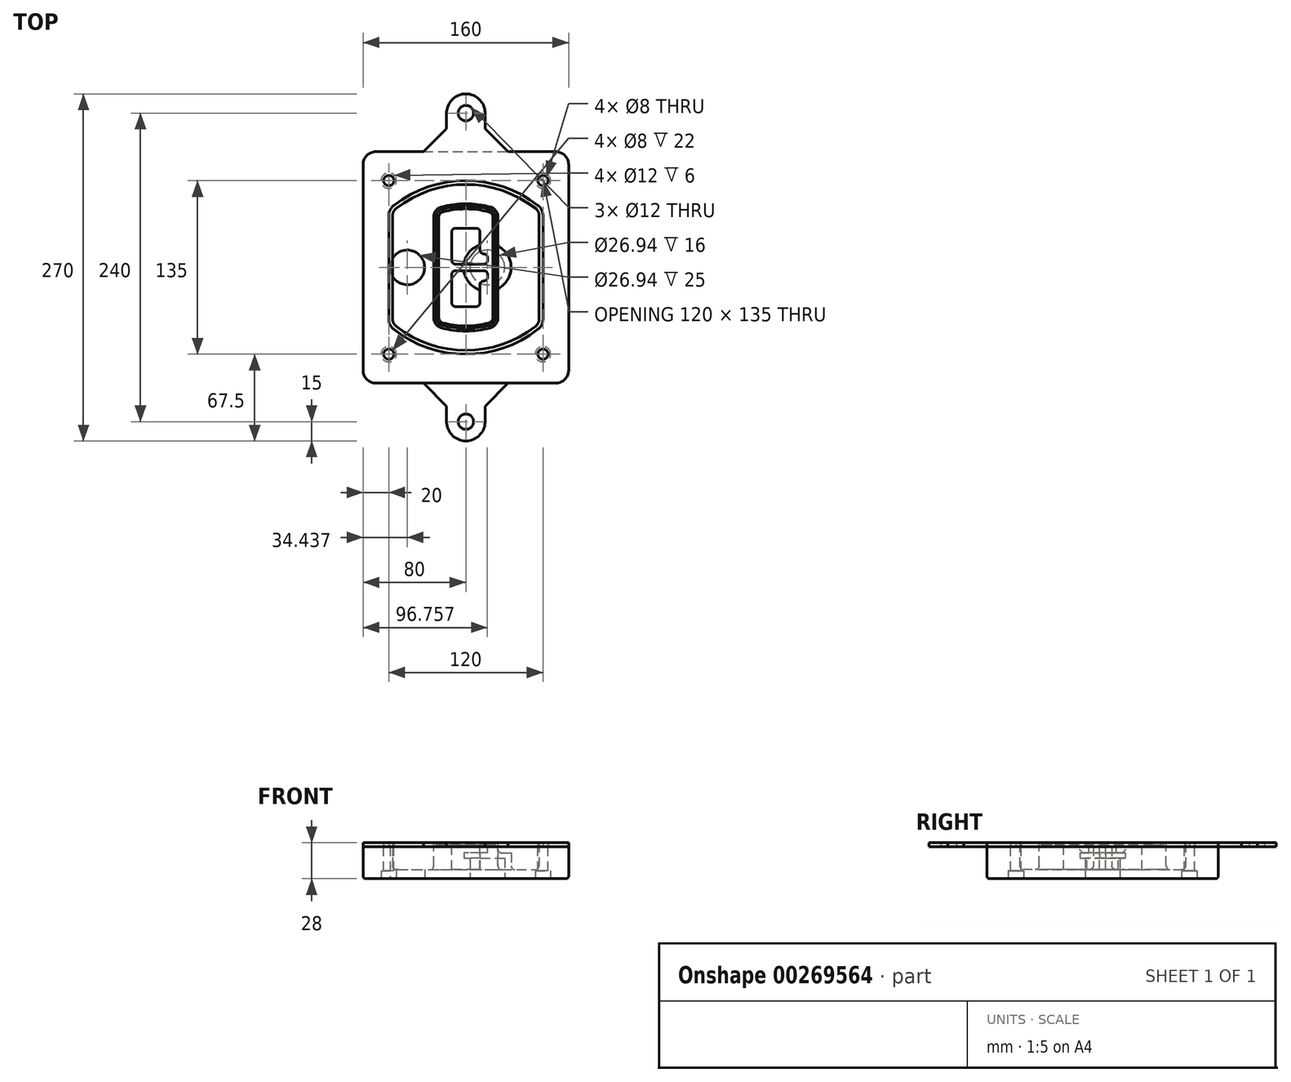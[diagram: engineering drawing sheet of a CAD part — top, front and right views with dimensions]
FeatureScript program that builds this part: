
annotation { "Feature Type Name" : "Feature", "Feature Type Description" : "" }
export const myFeature = defineFeature(function(context is Context, id is Id, definition is map)
    precondition{}
    {
        {
            var Q0;
            Q0=qCreatedBy(makeId("Top.planeOp"),FACE);
            var sketch = newSketch(context, id + "F0", { "sketchPlane" : qUnion([Q0])});
            skPoint(sketch, "E0.rect.middle", {"position": v(0, 0) * mm});
            skLineSegment(sketch, "E1.bottom", {"start": v(-70, -90) * mm, "end": v(70, -90) * mm});
            skLineSegment(sketch, "E1.top", {"start": v(-70, 90) * mm, "end": v(70, 90) * mm});
            skLineSegment(sketch, "E1.left", {"start": v(-80, -80) * mm, "end": v(-80, 80) * mm});
            skLineSegment(sketch, "E1.right", {"start": v(80, -80) * mm, "end": v(80, 80) * mm});
            skLineSegment(sketch, "E2", {"start": v(-80, 90) * mm, "end": v(80, -90) * mm, "construction": true});
            skLineSegment(sketch, "E3", {"start": v(80, 90) * mm, "end": v(-80, -90) * mm, "construction": true});
            skCircle(sketch, "E4", {"center": v(-60, 67.5) * mm, "radius": 4 * mm});
            skCircle(sketch, "E5", {"center": v(60, 67.5) * mm, "radius": 4 * mm});
            skCircle(sketch, "E6", {"center": v(60, -67.5) * mm, "radius": 4 * mm});
            skCircle(sketch, "E7", {"center": v(-60, -67.5) * mm, "radius": 4 * mm});
            skLineSegment(sketch, "E8", {"start": v(-60, 67.5) * mm, "end": v(60, 67.5) * mm, "construction": true});
            skLineSegment(sketch, "E9", {"start": v(60, 67.5) * mm, "end": v(60, -67.5) * mm, "construction": true});
            skLineSegment(sketch, "E10", {"start": v(60, -67.5) * mm, "end": v(-60, -67.5) * mm, "construction": true});
            skLineSegment(sketch, "E11", {"start": v(-60, -67.5) * mm, "end": v(-60, 67.5) * mm, "construction": true});
            skLineSegment(sketch, "E12", {"start": v(-60, 40.3) * mm, "end": v(-60, -40.3) * mm});
            skLineSegment(sketch, "E13", {"start": v(60, 40.3) * mm, "end": v(60, -40.3) * mm});
            skArc(sketch, "E14", {"start": v(56.15, 48.18) * mm, "mid": v(0, 67.5) * mm, "end": v(-56.15, 48.18) * mm});
            skArc(sketch, "E15", {"start": v(-56.15, -48.18) * mm, "mid": v(0, -67.5) * mm, "end": v(56.15, -48.18) * mm});
            skLineSegment(sketch, "E16", {"start": v(-60, 0) * mm, "end": v(60, 0) * mm, "construction": true});
            skPoint(sketch, "E17.visualSharp", {"position": v(-60, -45) * mm});
            skArc(sketch, "E17.filletArc", {"start": v(-60, -40.3) * mm, "mid": v(-58.99, -44.68) * mm, "end": v(-56.15, -48.18) * mm});
            skPoint(sketch, "E18.visualSharp", {"position": v(-60, 45) * mm});
            skArc(sketch, "E18.filletArc", {"start": v(-56.15, 48.18) * mm, "mid": v(-58.99, 44.68) * mm, "end": v(-60, 40.3) * mm});
            skPoint(sketch, "E19.visualSharp", {"position": v(60, 45) * mm});
            skArc(sketch, "E19.filletArc", {"start": v(60, 40.3) * mm, "mid": v(58.99, 44.68) * mm, "end": v(56.15, 48.18) * mm});
            skPoint(sketch, "E20.visualSharp", {"position": v(60, -45) * mm});
            skArc(sketch, "E20.filletArc", {"start": v(56.15, -48.18) * mm, "mid": v(58.99, -44.68) * mm, "end": v(60, -40.3) * mm});
            skPoint(sketch, "E21.visualSharp", {"position": v(-80, 90) * mm});
            skArc(sketch, "E21.filletArc", {"start": v(-70, 90) * mm, "mid": v(-77.07, 87.07) * mm, "end": v(-80, 80) * mm});
            skPoint(sketch, "E22.visualSharp", {"position": v(80, 90) * mm});
            skArc(sketch, "E22.filletArc", {"start": v(80, 80) * mm, "mid": v(77.07, 87.07) * mm, "end": v(70, 90) * mm});
            skPoint(sketch, "E23.visualSharp", {"position": v(80, -90) * mm});
            skArc(sketch, "E23.filletArc", {"start": v(70, -90) * mm, "mid": v(77.07, -87.07) * mm, "end": v(80, -80) * mm});
            skPoint(sketch, "E24.visualSharp", {"position": v(-80, -90) * mm});
            skArc(sketch, "E24.filletArc", {"start": v(-80, -80) * mm, "mid": v(-77.07, -87.07) * mm, "end": v(-70, -90) * mm});
            skArc(sketch, "E25.0", {"start": v(57, 40.3) * mm, "mid": v(56.3, 43.36) * mm, "end": v(54.3, 45.81) * mm});
            skLineSegment(sketch, "E25.1", {"start": v(57, 40.3) * mm, "end": v(57, -40.3) * mm});
            skArc(sketch, "E25.2", {"start": v(54.3, -45.81) * mm, "mid": v(56.3, -43.36) * mm, "end": v(57, -40.3) * mm});
            skArc(sketch, "E25.3", {"start": v(-54.3, -45.81) * mm, "mid": v(0, -64.5) * mm, "end": v(54.3, -45.81) * mm});
            skArc(sketch, "E25.4", {"start": v(-57, -40.3) * mm, "mid": v(-56.3, -43.36) * mm, "end": v(-54.3, -45.81) * mm});
            skArc(sketch, "E25.5", {"start": v(54.3, 45.81) * mm, "mid": v(0, 64.5) * mm, "end": v(-54.3, 45.81) * mm});
            skLineSegment(sketch, "E25.6", {"start": v(-57, 40.3) * mm, "end": v(-57, -40.3) * mm});
            skArc(sketch, "E25.7", {"start": v(-54.3, 45.81) * mm, "mid": v(-56.3, 43.36) * mm, "end": v(-57, 40.3) * mm});
            skArc(sketch, "E26.0", {"start": v(-58.62, 51.33) * mm, "mid": v(-62.58, 46.43) * mm, "end": v(-64, 40.3) * mm});
            skArc(sketch, "E26.1", {"start": v(58.62, 51.33) * mm, "mid": v(0, 71.5) * mm, "end": v(-58.62, 51.33) * mm});
            skArc(sketch, "E26.2", {"start": v(64, 40.3) * mm, "mid": v(62.58, 46.43) * mm, "end": v(58.62, 51.33) * mm});
            skLineSegment(sketch, "E26.3", {"start": v(64, 40.3) * mm, "end": v(64, -40.3) * mm});
            skArc(sketch, "E26.4", {"start": v(58.62, -51.33) * mm, "mid": v(62.58, -46.43) * mm, "end": v(64, -40.3) * mm});
            skLineSegment(sketch, "E26.5", {"start": v(-64, 40.3) * mm, "end": v(-64, -40.3) * mm});
            skArc(sketch, "E26.6", {"start": v(-58.62, -51.33) * mm, "mid": v(0, -71.5) * mm, "end": v(58.62, -51.33) * mm});
            skArc(sketch, "E26.7", {"start": v(-64, -40.3) * mm, "mid": v(-62.58, -46.43) * mm, "end": v(-58.62, -51.33) * mm});
            skSolve(sketch);
        }
        {
            var Q0;
            Q0=makeQuery(id+"F0.imprint","IMPRINT",FACE,{"disambiguationData":[TD([[makeQuery(id+"F0.imprint","IMPRINT",EDGE,{"derivedFrom":sQuery(id+"F0.wireOp",EDGE,"E1.bottom")}),1.0]])]});
            var Q1;
            Q1=makeQuery(id+"F0.imprint","IMPRINT",FACE,{"disambiguationData":[TD([[makeQuery(id+"F0.imprint","IMPRINT",EDGE,{"derivedFrom":sQuery(id+"F0.wireOp",EDGE,"E12")}),1.0]])]});
            var Q2;
            Q2=makeQuery(id+"F0.imprint","IMPRINT",FACE,{"disambiguationData":[TD([[makeQuery(id+"F0.imprint","IMPRINT",EDGE,{"derivedFrom":sQuery(id+"F0.wireOp",EDGE,"E25.0")}),1.0]])]});
            var Q3;
            Q3=makeQuery(id+"F0.imprint","IMPRINT",FACE,{"disambiguationData":[TD([[makeQuery(id+"F0.imprint","IMPRINT",EDGE,{"derivedFrom":sQuery(id+"F0.wireOp",EDGE,"E12")}),-1.0]])]});
            extrude(context, id + "F1", {"entities" : qUnion([Q0, Q1, Q2, Q3]), "oppositeDirection" : true, "depth" : 25 * mm});
        }
        {
            var Q0;
            Q0=makeQuery(id+"F0.imprint","IMPRINT",FACE,{"disambiguationData":[TD([[makeQuery(id+"F0.imprint","IMPRINT",EDGE,{"derivedFrom":sQuery(id+"F0.wireOp",EDGE,"E12")}),1.0]])]});
            extrude(context, id + "F2", {"entities" : qUnion([Q0]), "operationType" : NewBodyOperationType.ADD, "depth" : 3 * mm});
        }
        {
            var Q0;
            Q0=makeQuery(id+"F0.imprint","IMPRINT",FACE,{"disambiguationData":[TD([[makeQuery(id+"F0.imprint","IMPRINT",EDGE,{"derivedFrom":sQuery(id+"F0.wireOp",EDGE,"E25.0")}),1.0]])]});
            extrude(context, id + "F3", {"entities" : qUnion([Q0]), "operationType" : NewBodyOperationType.REMOVE, "oppositeDirection" : true, "depth" : 18 * mm});
        }
        {
            var Q0;
            Q0=makeQuery(id+"F2.opExtrude","CAP_FACE",FACE,{"disambiguationData":[OSD([sQuery(id+"F0.wireOp",EDGE,"E12"),sQuery(id+"F0.wireOp",EDGE,"E13"),sQuery(id+"F0.wireOp",EDGE,"E14"),sQuery(id+"F0.wireOp",EDGE,"E15"),sQuery(id+"F0.wireOp",EDGE,"E17.filletArc"),sQuery(id+"F0.wireOp",EDGE,"E18.filletArc"),sQuery(id+"F0.wireOp",EDGE,"E19.filletArc"),sQuery(id+"F0.wireOp",EDGE,"E20.filletArc"),sQuery(id+"F0.wireOp",EDGE,"E25.0"),sQuery(id+"F0.wireOp",EDGE,"E25.1"),sQuery(id+"F0.wireOp",EDGE,"E25.2"),sQuery(id+"F0.wireOp",EDGE,"E25.3"),sQuery(id+"F0.wireOp",EDGE,"E25.4"),sQuery(id+"F0.wireOp",EDGE,"E25.5"),sQuery(id+"F0.wireOp",EDGE,"E25.6"),sQuery(id+"F0.wireOp",EDGE,"E25.7")])],"isStart":false});
            var sketch = newSketch(context, id + "F4", { "sketchPlane" : qUnion([Q0])});
            skArc(sketch, "E27.0", {"start": v(-19.08, -46.97) * mm, "mid": v(0, -49.5) * mm, "end": v(19.08, -46.97) * mm});
            skArc(sketch, "E28.0", {"start": v(19.08, 46.97) * mm, "mid": v(0, 49.5) * mm, "end": v(-19.08, 46.97) * mm});
            skLineSegment(sketch, "E29", {"start": v(-25, 39.25) * mm, "end": v(-25, -39.25) * mm});
            skLineSegment(sketch, "E30", {"start": v(25, 39.25) * mm, "end": v(25, -39.25) * mm});
            skLineSegment(sketch, "E31", {"start": v(-25, 45.1) * mm, "end": v(25, 45.1) * mm, "construction": true});
            skLineSegment(sketch, "E32", {"start": v(-25, -45.1) * mm, "end": v(25, -45.1) * mm, "construction": true});
            skPoint(sketch, "E33.visualSharp", {"position": v(-25, 45.1) * mm});
            skArc(sketch, "E33.filletArc", {"start": v(-19.08, 46.97) * mm, "mid": v(-23.35, 44.11) * mm, "end": v(-25, 39.25) * mm});
            skPoint(sketch, "E34.visualSharp", {"position": v(25, 45.1) * mm});
            skArc(sketch, "E34.filletArc", {"start": v(25, 39.25) * mm, "mid": v(23.35, 44.11) * mm, "end": v(19.08, 46.97) * mm});
            skPoint(sketch, "E35.visualSharp", {"position": v(25, -45.1) * mm});
            skArc(sketch, "E35.filletArc", {"start": v(19.08, -46.97) * mm, "mid": v(23.35, -44.11) * mm, "end": v(25, -39.25) * mm});
            skPoint(sketch, "E36.visualSharp", {"position": v(-25, -45.1) * mm});
            skArc(sketch, "E36.filletArc", {"start": v(-25, -39.25) * mm, "mid": v(-23.35, -44.11) * mm, "end": v(-19.08, -46.97) * mm});
            skArc(sketch, "E37.0", {"start": v(54.3, 45.81) * mm, "mid": v(0, 64.5) * mm, "end": v(-54.3, 45.81) * mm});
            skArc(sketch, "E37.1", {"start": v(-54.3, 45.81) * mm, "mid": v(-56.3, 43.36) * mm, "end": v(-57, 40.3) * mm});
            skLineSegment(sketch, "E37.2", {"start": v(-57, 40.3) * mm, "end": v(-57, -40.3) * mm});
            skArc(sketch, "E37.3", {"start": v(-57, -40.3) * mm, "mid": v(-56.3, -43.36) * mm, "end": v(-54.3, -45.81) * mm});
            skArc(sketch, "E37.4", {"start": v(-54.3, -45.81) * mm, "mid": v(0, -64.5) * mm, "end": v(54.3, -45.81) * mm});
            skArc(sketch, "E37.5", {"start": v(54.3, -45.81) * mm, "mid": v(56.3, -43.36) * mm, "end": v(57, -40.3) * mm});
            skLineSegment(sketch, "E37.6", {"start": v(57, 40.3) * mm, "end": v(57, -40.3) * mm});
            skArc(sketch, "E37.7", {"start": v(57, 40.3) * mm, "mid": v(56.3, 43.36) * mm, "end": v(54.3, 45.81) * mm});
            skLineSegment(sketch, "E38.0", {"start": v(23, 39.25) * mm, "end": v(23, -39.25) * mm});
            skArc(sketch, "E38.1", {"start": v(18.56, -45.04) * mm, "mid": v(21.76, -42.9) * mm, "end": v(23, -39.25) * mm});
            skArc(sketch, "E38.2", {"start": v(-18.56, -45.04) * mm, "mid": v(0, -47.5) * mm, "end": v(18.56, -45.04) * mm});
            skArc(sketch, "E38.3", {"start": v(-23, -39.25) * mm, "mid": v(-21.76, -42.9) * mm, "end": v(-18.56, -45.04) * mm});
            skLineSegment(sketch, "E38.4", {"start": v(-23, 39.25) * mm, "end": v(-23, -39.25) * mm});
            skArc(sketch, "E38.5", {"start": v(23, 39.25) * mm, "mid": v(21.76, 42.9) * mm, "end": v(18.56, 45.04) * mm});
            skArc(sketch, "E38.6", {"start": v(-18.56, 45.04) * mm, "mid": v(-21.76, 42.9) * mm, "end": v(-23, 39.25) * mm});
            skArc(sketch, "E38.7", {"start": v(18.56, 45.04) * mm, "mid": v(0, 47.5) * mm, "end": v(-18.56, 45.04) * mm});
            skArc(sketch, "E39.0", {"start": v(21, 39.25) * mm, "mid": v(20.18, 41.68) * mm, "end": v(18.04, 43.1) * mm});
            skLineSegment(sketch, "E39.1", {"start": v(21, 39.25) * mm, "end": v(21, -39.25) * mm});
            skArc(sketch, "E39.2", {"start": v(18.04, -43.1) * mm, "mid": v(20.18, -41.68) * mm, "end": v(21, -39.25) * mm});
            skArc(sketch, "E39.3", {"start": v(-18.04, -43.1) * mm, "mid": v(0, -45.5) * mm, "end": v(18.04, -43.1) * mm});
            skArc(sketch, "E39.4", {"start": v(-21, -39.25) * mm, "mid": v(-20.18, -41.68) * mm, "end": v(-18.04, -43.1) * mm});
            skArc(sketch, "E39.5", {"start": v(18.04, 43.1) * mm, "mid": v(0, 45.5) * mm, "end": v(-18.04, 43.1) * mm});
            skLineSegment(sketch, "E39.6", {"start": v(-21, 39.25) * mm, "end": v(-21, -39.25) * mm});
            skArc(sketch, "E39.7", {"start": v(-18.04, 43.1) * mm, "mid": v(-20.18, 41.68) * mm, "end": v(-21, 39.25) * mm});
            skLineSegment(sketch, "E40", {"start": v(-25, 0) * mm, "end": v(25, 0) * mm, "construction": true});
            skLineSegment(sketch, "E41", {"start": v(-11, 5.5) * mm, "end": v(-11, 27.5) * mm});
            skLineSegment(sketch, "E42", {"start": v(-8, 30.5) * mm, "end": v(8, 30.5) * mm});
            skLineSegment(sketch, "E43", {"start": v(11, 27.5) * mm, "end": v(11, 13.5) * mm});
            skLineSegment(sketch, "E44", {"start": v(14, 10.5) * mm, "end": v(14, 10.5) * mm});
            skLineSegment(sketch, "E45", {"start": v(17, 7.5) * mm, "end": v(17, 5.5) * mm});
            skLineSegment(sketch, "E46", {"start": v(14, 2.5) * mm, "end": v(-8, 2.5) * mm});
            skPoint(sketch, "E47.visualSharp", {"position": v(-11, 30.5) * mm});
            skArc(sketch, "E47.filletArc", {"start": v(-8, 30.5) * mm, "mid": v(-10.12, 29.62) * mm, "end": v(-11, 27.5) * mm});
            skPoint(sketch, "E48.visualSharp", {"position": v(11, 30.5) * mm});
            skArc(sketch, "E48.filletArc", {"start": v(11, 27.5) * mm, "mid": v(10.12, 29.62) * mm, "end": v(8, 30.5) * mm});
            skPoint(sketch, "E49.visualSharp", {"position": v(11, 10.5) * mm});
            skArc(sketch, "E49.filletArc", {"start": v(11, 13.5) * mm, "mid": v(11.88, 11.38) * mm, "end": v(14, 10.5) * mm});
            skPoint(sketch, "E50.visualSharp", {"position": v(17, 10.5) * mm});
            skArc(sketch, "E50.filletArc", {"start": v(17, 7.5) * mm, "mid": v(16.12, 9.62) * mm, "end": v(14, 10.5) * mm});
            skPoint(sketch, "E51.visualSharp", {"position": v(17, 2.5) * mm});
            skArc(sketch, "E51.filletArc", {"start": v(14, 2.5) * mm, "mid": v(16.12, 3.38) * mm, "end": v(17, 5.5) * mm});
            skPoint(sketch, "E52.visualSharp", {"position": v(-11, 2.5) * mm});
            skArc(sketch, "E52.filletArc", {"start": v(-11, 5.5) * mm, "mid": v(-10.12, 3.38) * mm, "end": v(-8, 2.5) * mm});
            skLineSegment(sketch, "E53.0.MirrorCS", {"start": v(14, -2.5) * mm, "end": v(-8, -2.5) * mm});
            skArc(sketch, "E54.0.MirrorCS", {"start": v(-11, -5.5) * mm, "mid": v(-10.12, -3.38) * mm, "end": v(-8, -2.5) * mm});
            skLineSegment(sketch, "E55.0.MirrorCS", {"start": v(-11, -5.5) * mm, "end": v(-11, -27.5) * mm});
            skArc(sketch, "E56.0.MirrorCS", {"start": v(-8, -30.5) * mm, "mid": v(-10.12, -29.62) * mm, "end": v(-11, -27.5) * mm});
            skLineSegment(sketch, "E57.0.MirrorCS", {"start": v(-8, -30.5) * mm, "end": v(8, -30.5) * mm});
            skArc(sketch, "E58.0.MirrorCS", {"start": v(11, -27.5) * mm, "mid": v(10.12, -29.62) * mm, "end": v(8, -30.5) * mm});
            skLineSegment(sketch, "E59.0.MirrorCS", {"start": v(11, -27.5) * mm, "end": v(11, -13.5) * mm});
            skArc(sketch, "E60.0.MirrorCS", {"start": v(11, -13.5) * mm, "mid": v(11.88, -11.38) * mm, "end": v(14, -10.5) * mm});
            skArc(sketch, "E61.0.MirrorCS", {"start": v(17, -7.5) * mm, "mid": v(16.12, -9.62) * mm, "end": v(14, -10.5) * mm});
            skLineSegment(sketch, "E62.0.MirrorCS", {"start": v(17, -7.5) * mm, "end": v(17, -5.5) * mm});
            skArc(sketch, "E63.0.MirrorCS", {"start": v(14, -2.5) * mm, "mid": v(16.12, -3.38) * mm, "end": v(17, -5.5) * mm});
            skSolve(sketch);
        }
        {
            var Q0;
            Q0=makeQuery(id+"F4.imprint","IMPRINT",FACE,{"disambiguationData":[TD([[makeQuery(id+"F4.imprint","IMPRINT",EDGE,{"derivedFrom":sQuery(id+"F4.wireOp",EDGE,"E27.0")}),1.0]])]});
            var Q1;
            Q1=makeQuery(id+"F4.imprint","IMPRINT",FACE,{"disambiguationData":[TD([[makeQuery(id+"F4.imprint","IMPRINT",EDGE,{"derivedFrom":sQuery(id+"F4.wireOp",EDGE,"E38.0")}),-1.0]])]});
            var Q2;
            Q2=makeQuery(id+"F4.imprint","IMPRINT",FACE,{"disambiguationData":[TD([[makeQuery(id+"F4.imprint","IMPRINT",EDGE,{"derivedFrom":sQuery(id+"F4.wireOp",EDGE,"E39.0")}),1.0]])]});
            extrude(context, id + "F5", {"entities" : qUnion([Q0, Q1, Q2]), "operationType" : NewBodyOperationType.ADD, "endBound" : BoundingType.UP_TO_NEXT, "oppositeDirection" : true, "depth" : 25 * mm});
        }
        {
            var Q0;
            Q0=makeQuery(id+"F4.imprint","IMPRINT",FACE,{"disambiguationData":[TD([[makeQuery(id+"F4.imprint","IMPRINT",EDGE,{"derivedFrom":sQuery(id+"F4.wireOp",EDGE,"E38.0")}),-1.0]])]});
            extrude(context, id + "F6", {"entities" : qUnion([Q0]), "operationType" : NewBodyOperationType.REMOVE, "oppositeDirection" : true, "depth" : 2 * mm});
        }
        {
            var Q0;
            Q0=makeQuery(id+"F1.opExtrude","CAP_FACE",FACE,{"disambiguationData":[OSD([sQuery(id+"F0.wireOp",EDGE,"E1.bottom"),sQuery(id+"F0.wireOp",EDGE,"E1.top"),sQuery(id+"F0.wireOp",EDGE,"E1.left"),sQuery(id+"F0.wireOp",EDGE,"E1.right"),sQuery(id+"F0.wireOp",EDGE,"E4"),sQuery(id+"F0.wireOp",EDGE,"E5"),sQuery(id+"F0.wireOp",EDGE,"E6"),sQuery(id+"F0.wireOp",EDGE,"E7"),sQuery(id+"F0.wireOp",EDGE,"E21.filletArc"),sQuery(id+"F0.wireOp",EDGE,"E22.filletArc"),sQuery(id+"F0.wireOp",EDGE,"E23.filletArc"),sQuery(id+"F0.wireOp",EDGE,"E24.filletArc")])],"isStart":false});
            var sketch = newSketch(context, id + "F7", { "sketchPlane" : qUnion([Q0])});
            skCircle(sketch, "E64", {"center": v(16.76, 0) * mm, "radius": 13.47 * mm});
            skCircle(sketch, "E65", {"center": v(-45.56, 0) * mm, "radius": 13.47 * mm});
            skLineSegment(sketch, "E66", {"start": v(80, 0) * mm, "end": v(-80, 0) * mm});
            skCircle(sketch, "E67", {"center": v(16.76, 0) * mm, "radius": 18.47 * mm});
            skCircle(sketch, "E68", {"center": v(60, -67.5) * mm, "radius": 6 * mm});
            skCircle(sketch, "E69", {"center": v(-60, -67.5) * mm, "radius": 6 * mm});
            skCircle(sketch, "E70", {"center": v(-60, 67.5) * mm, "radius": 6 * mm});
            skCircle(sketch, "E71", {"center": v(60, 67.5) * mm, "radius": 6 * mm});
            skSolve(sketch);
        }
        {
            var Q0;
            {var subQ1=sQuery(id+"F7.wireOp",EDGE,"E66");var subQ4=sQuery(id+"F7.wireOp",EDGE,"E64");var subQ6=makeQuery(id+"F7.imprint","INTERSECT",VERTEX,{"disambiguationData":[OD(0.0)],"derivedFrom":[subQ4,subQ1]});Q0=makeQuery(id+"F7.imprint","IMPRINT",FACE,{"disambiguationData":[TD([[makeQuery(id+"F7.imprint","IMPRINT",EDGE,{"disambiguationData":[TD([[subQ6,-1.0]])],"derivedFrom":subQ4}),-1.0]])]});}
            var Q1;
            {var subQ0=sQuery(id+"F7.wireOp",EDGE,"E66");var subQ1=sQuery(id+"F7.wireOp",EDGE,"E64");var subQ3=makeQuery(id+"F7.imprint","INTERSECT",VERTEX,{"disambiguationData":[OD(0.0)],"derivedFrom":[subQ1,subQ0]});Q1=makeQuery(id+"F7.imprint","IMPRINT",FACE,{"disambiguationData":[TD([[makeQuery(id+"F7.imprint","IMPRINT",EDGE,{"disambiguationData":[TD([[subQ3,-1.0]])],"derivedFrom":subQ1}),1.0]])]});}
            var Q2;
            {var subQ0=sQuery(id+"F7.wireOp",EDGE,"E66");var subQ1=sQuery(id+"F7.wireOp",EDGE,"E64");var subQ3=makeQuery(id+"F7.imprint","INTERSECT",VERTEX,{"disambiguationData":[OD(0.0)],"derivedFrom":[subQ1,subQ0]});Q2=makeQuery(id+"F7.imprint","IMPRINT",FACE,{"disambiguationData":[TD([[makeQuery(id+"F7.imprint","IMPRINT",EDGE,{"disambiguationData":[TD([[subQ3,1.0]])],"derivedFrom":subQ1}),1.0]])]});}
            var Q3;
            {var subQ1=sQuery(id+"F7.wireOp",EDGE,"E66");var subQ4=sQuery(id+"F7.wireOp",EDGE,"E64");var subQ6=makeQuery(id+"F7.imprint","INTERSECT",VERTEX,{"disambiguationData":[OD(0.0)],"derivedFrom":[subQ4,subQ1]});Q3=makeQuery(id+"F7.imprint","IMPRINT",FACE,{"disambiguationData":[TD([[makeQuery(id+"F7.imprint","IMPRINT",EDGE,{"disambiguationData":[TD([[subQ6,1.0]])],"derivedFrom":subQ4}),-1.0]])]});}
            extrude(context, id + "F8", {"entities" : qUnion([Q0, Q1, Q2, Q3]), "operationType" : NewBodyOperationType.ADD, "oppositeDirection" : true, "depth" : 20 * mm});
        }
        {
            var Q0;
            {var subQ0=sQuery(id+"F7.wireOp",EDGE,"E66");var subQ1=sQuery(id+"F7.wireOp",EDGE,"E64");var subQ3=makeQuery(id+"F7.imprint","INTERSECT",VERTEX,{"disambiguationData":[OD(0.0)],"derivedFrom":[subQ1,subQ0]});Q0=makeQuery(id+"F7.imprint","IMPRINT",FACE,{"disambiguationData":[TD([[makeQuery(id+"F7.imprint","IMPRINT",EDGE,{"disambiguationData":[TD([[subQ3,-1.0]])],"derivedFrom":subQ1}),1.0]])]});}
            var Q1;
            {var subQ0=sQuery(id+"F7.wireOp",EDGE,"E66");var subQ1=sQuery(id+"F7.wireOp",EDGE,"E64");var subQ3=makeQuery(id+"F7.imprint","INTERSECT",VERTEX,{"disambiguationData":[OD(0.0)],"derivedFrom":[subQ1,subQ0]});Q1=makeQuery(id+"F7.imprint","IMPRINT",FACE,{"disambiguationData":[TD([[makeQuery(id+"F7.imprint","IMPRINT",EDGE,{"disambiguationData":[TD([[subQ3,1.0]])],"derivedFrom":subQ1}),1.0]])]});}
            extrude(context, id + "F9", {"entities" : qUnion([Q0, Q1]), "operationType" : NewBodyOperationType.REMOVE, "oppositeDirection" : true, "depth" : 16 * mm});
        }
        {
            var Q0;
            {var subQ0=sQuery(id+"F7.wireOp",EDGE,"E66");var subQ1=sQuery(id+"F7.wireOp",EDGE,"E65");var subQ3=makeQuery(id+"F7.imprint","INTERSECT",VERTEX,{"disambiguationData":[OD(0.0)],"derivedFrom":[subQ1,subQ0]});Q0=makeQuery(id+"F7.imprint","IMPRINT",FACE,{"disambiguationData":[TD([[makeQuery(id+"F7.imprint","IMPRINT",EDGE,{"disambiguationData":[TD([[subQ3,-1.0]])],"derivedFrom":subQ1}),1.0]])]});}
            var Q1;
            {var subQ0=sQuery(id+"F7.wireOp",EDGE,"E66");var subQ1=sQuery(id+"F7.wireOp",EDGE,"E65");var subQ3=makeQuery(id+"F7.imprint","INTERSECT",VERTEX,{"disambiguationData":[OD(0.0)],"derivedFrom":[subQ1,subQ0]});Q1=makeQuery(id+"F7.imprint","IMPRINT",FACE,{"disambiguationData":[TD([[makeQuery(id+"F7.imprint","IMPRINT",EDGE,{"disambiguationData":[TD([[subQ3,1.0]])],"derivedFrom":subQ1}),1.0]])]});}
            extrude(context, id + "F10", {"entities" : qUnion([Q0, Q1]), "operationType" : NewBodyOperationType.REMOVE, "oppositeDirection" : true, "depth" : 25 * mm});
        }
        {
            var Q0;
            Q0=makeQuery(id+"F7.imprint","IMPRINT",FACE,{"disambiguationData":[TD([[makeQuery(id+"F7.imprint","IMPRINT",EDGE,{"derivedFrom":sQuery(id+"F7.wireOp",EDGE,"E68")}),1.0]])]});
            var Q1;
            Q1=makeQuery(id+"F7.imprint","IMPRINT",FACE,{"disambiguationData":[TD([[makeQuery(id+"F7.imprint","IMPRINT",EDGE,{"derivedFrom":makeQuery(id+"F1.opExtrude","CAP_EDGE",EDGE,{"disambiguationData":[OSD([sQuery(id+"F0.wireOp",EDGE,"E5")])],"isStart":false})}),-1.0]])]});
            var Q2;
            Q2=makeQuery(id+"F7.imprint","IMPRINT",FACE,{"disambiguationData":[TD([[makeQuery(id+"F7.imprint","IMPRINT",EDGE,{"derivedFrom":sQuery(id+"F7.wireOp",EDGE,"E69")}),1.0]])]});
            var Q3;
            Q3=makeQuery(id+"F7.imprint","IMPRINT",FACE,{"disambiguationData":[TD([[makeQuery(id+"F7.imprint","IMPRINT",EDGE,{"derivedFrom":makeQuery(id+"F1.opExtrude","CAP_EDGE",EDGE,{"disambiguationData":[OSD([sQuery(id+"F0.wireOp",EDGE,"E4")])],"isStart":false})}),-1.0]])]});
            var Q4;
            Q4=makeQuery(id+"F7.imprint","IMPRINT",FACE,{"disambiguationData":[TD([[makeQuery(id+"F7.imprint","IMPRINT",EDGE,{"derivedFrom":sQuery(id+"F7.wireOp",EDGE,"E70")}),1.0]])]});
            var Q5;
            Q5=makeQuery(id+"F7.imprint","IMPRINT",FACE,{"disambiguationData":[TD([[makeQuery(id+"F7.imprint","IMPRINT",EDGE,{"derivedFrom":makeQuery(id+"F1.opExtrude","CAP_EDGE",EDGE,{"disambiguationData":[OSD([sQuery(id+"F0.wireOp",EDGE,"E7")])],"isStart":false})}),-1.0]])]});
            var Q6;
            Q6=makeQuery(id+"F7.imprint","IMPRINT",FACE,{"disambiguationData":[TD([[makeQuery(id+"F7.imprint","IMPRINT",EDGE,{"derivedFrom":sQuery(id+"F7.wireOp",EDGE,"E71")}),1.0]])]});
            var Q7;
            Q7=makeQuery(id+"F7.imprint","IMPRINT",FACE,{"disambiguationData":[TD([[makeQuery(id+"F7.imprint","IMPRINT",EDGE,{"derivedFrom":makeQuery(id+"F1.opExtrude","CAP_EDGE",EDGE,{"disambiguationData":[OSD([sQuery(id+"F0.wireOp",EDGE,"E6")])],"isStart":false})}),-1.0]])]});
            extrude(context, id + "F11", {"entities" : qUnion([Q0, Q1, Q2, Q3, Q4, Q5, Q6, Q7]), "operationType" : NewBodyOperationType.REMOVE, "oppositeDirection" : true, "depth" : 6 * mm});
        }
        {
            var Q0;
            Q0=makeQuery(id+"F9.boolean.opBoolean","COPY",FACE,{"derivedFrom":makeQuery(id+"F9.opExtrude","CAP_FACE",FACE,{"disambiguationData":[OSD([sQuery(id+"F7.wireOp",EDGE,"E64")])],"isStart":false})});
            var sketch = newSketch(context, id + "F12", { "sketchPlane" : qUnion([Q0])});
            skArc(sketch, "E72.0", {"start": v(11, 17.55) * mm, "mid": v(2.57, 11.82) * mm, "end": v(-1.54, 2.5) * mm});
            skArc(sketch, "E72.1", {"start": v(-1.54, -2.5) * mm, "mid": v(2.57, -11.82) * mm, "end": v(11, -17.55) * mm});
            skLineSegment(sketch, "E73", {"start": v(-1.54, -2.5) * mm, "end": v(14, -2.5) * mm});
            skLineSegment(sketch, "E74.0", {"start": v(14, 2.5) * mm, "end": v(-1.54, 2.5) * mm});
            skArc(sketch, "E74.1", {"start": v(14, 2.5) * mm, "mid": v(16.12, 3.38) * mm, "end": v(17, 5.5) * mm});
            skLineSegment(sketch, "E74.2", {"start": v(17, 7.5) * mm, "end": v(17, 5.5) * mm});
            skArc(sketch, "E74.3", {"start": v(17, 7.5) * mm, "mid": v(16.12, 9.62) * mm, "end": v(14, 10.5) * mm});
            skArc(sketch, "E74.4", {"start": v(11, 13.5) * mm, "mid": v(11.88, 11.38) * mm, "end": v(14, 10.5) * mm});
            skLineSegment(sketch, "E74.5", {"start": v(11, 17.55) * mm, "end": v(11, 13.5) * mm});
            skLineSegment(sketch, "E74.7", {"start": v(14, -2.5) * mm, "end": v(-1.54, -2.5) * mm});
            skArc(sketch, "E74.8", {"start": v(14, -2.5) * mm, "mid": v(16.12, -3.38) * mm, "end": v(17, -5.5) * mm});
            skLineSegment(sketch, "E74.9", {"start": v(17, -7.5) * mm, "end": v(17, -5.5) * mm});
            skArc(sketch, "E74.10", {"start": v(17, -7.5) * mm, "mid": v(16.12, -9.62) * mm, "end": v(14, -10.5) * mm});
            skArc(sketch, "E74.11", {"start": v(11, -13.5) * mm, "mid": v(11.88, -11.38) * mm, "end": v(14, -10.5) * mm});
            skLineSegment(sketch, "E74.12", {"start": v(11, -17.55) * mm, "end": v(11, -13.5) * mm});
            skPoint(sketch, "E75.orphan", {"position": v(11, -27.5) * mm});
            skPoint(sketch, "E76.orphan", {"position": v(-8, -2.5) * mm});
            skPoint(sketch, "E77.orphan", {"position": v(-8, 2.5) * mm});
            skPoint(sketch, "E78.orphan", {"position": v(11, 27.5) * mm});
            skSolve(sketch);
        }
        {
            var Q0;
            {var subQ7=sQuery(id+"F12.wireOp",EDGE,"E72.0");var subQ14=sQuery(id+"F12.wireOp",EDGE,"E72.1");var subQ16=sQuery(id+"F12.wireOp",EDGE,"E74.1");var subQ18=sQuery(id+"F12.wireOp",EDGE,"E74.8");Q0=qUnion([makeQuery(id+"F12.imprint","IMPRINT",FACE,{"disambiguationData":[TD([[makeQuery(id+"F12.imprint","IMPRINT",EDGE,{"derivedFrom":subQ7}),1.0]])]}),makeQuery(id+"F12.imprint","IMPRINT",FACE,{"disambiguationData":[TD([[makeQuery(id+"F12.imprint","IMPRINT",EDGE,{"derivedFrom":subQ14}),1.0]])]}),makeQuery(id+"F12.imprint","IMPRINT",FACE,{"disambiguationData":[TD([[makeQuery(id+"F12.imprint","IMPRINT",EDGE,{"derivedFrom":subQ16}),1.0]])]}),makeQuery(id+"F12.imprint","IMPRINT",FACE,{"disambiguationData":[TD([[makeQuery(id+"F12.imprint","IMPRINT",EDGE,{"derivedFrom":subQ18}),-1.0]])]})]);}
            var Q1;
            Q1=makeQuery(id+"F5.boolean.opBoolean","SPLIT",FACE,{"disambiguationData":[TD([makeQuery(id+"F5.opExtrude","SWEPT_FACE",FACE,{"disambiguationData":[OSD([sQuery(id+"F4.wireOp",EDGE,"E41")])]})])],"derivedFrom":makeQuery(id+"F3.boolean.opBoolean","COPY",FACE,{"derivedFrom":makeQuery(id+"F3.opExtrude","CAP_FACE",FACE,{"disambiguationData":[OSD([sQuery(id+"F0.wireOp",EDGE,"E25.0"),sQuery(id+"F0.wireOp",EDGE,"E25.1"),sQuery(id+"F0.wireOp",EDGE,"E25.2"),sQuery(id+"F0.wireOp",EDGE,"E25.3"),sQuery(id+"F0.wireOp",EDGE,"E25.4"),sQuery(id+"F0.wireOp",EDGE,"E25.5"),sQuery(id+"F0.wireOp",EDGE,"E25.6"),sQuery(id+"F0.wireOp",EDGE,"E25.7")])],"isStart":false})})});
            extrude(context, id + "F13", {"entities" : qUnion([Q0]), "operationType" : NewBodyOperationType.REMOVE, "endBound" : BoundingType.UP_TO_SURFACE, "endBoundEntityFace" : qUnion([Q1]), "depth" : 25 * mm});
        }
        {
            var Q0;
            Q0=makeQuery(id+"F3.boolean.opBoolean","COPY",EDGE,{"derivedFrom":makeQuery(id+"F3.opExtrude","CAP_EDGE",EDGE,{"disambiguationData":[OSD([sQuery(id+"F0.wireOp",EDGE,"E25.6")])],"isStart":false})});
            var Q1;
            Q1=makeQuery(id+"F8.boolean.opBoolean","INTERSECT",EDGE,{"derivedFrom":[makeQuery(id+"F5.opExtrude","SWEPT_FACE",FACE,{"disambiguationData":[OSD([sQuery(id+"F4.wireOp",EDGE,"E30")])]}),makeQuery(id+"F8.opExtrude","CAP_FACE",FACE,{"disambiguationData":[OSD([sQuery(id+"F7.wireOp",EDGE,"E67")])],"isStart":false})]});
            var Q2;
            Q2=makeQuery(id+"F8.boolean.opBoolean","INTERSECT",EDGE,{"disambiguationData":[OD(1.0)],"derivedFrom":[makeQuery(id+"F5.opExtrude","SWEPT_FACE",FACE,{"disambiguationData":[OSD([sQuery(id+"F4.wireOp",EDGE,"E30")])]}),makeQuery(id+"F8.opExtrude","SWEPT_FACE",FACE,{"disambiguationData":[OSD([sQuery(id+"F7.wireOp",EDGE,"E67")])]})]});
            var Q3;
            {var subQ0=sQuery(id+"F4.wireOp",EDGE,"E30");Q3=makeQuery(id+"F8.boolean.opBoolean","SPLIT",EDGE,{"disambiguationData":[TD([makeQuery(id+"F5.opExtrude","SWEPT_FACE",FACE,{"disambiguationData":[OSD([sQuery(id+"F4.wireOp",EDGE,"E35.filletArc")])]})])],"derivedFrom":makeQuery(id+"F5.opExtrude","CAP_EDGE",EDGE,{"disambiguationData":[OSD([subQ0])],"isStart":false})});}
            var Q4;
            {var subQ0=sQuery(id+"F0.wireOp",EDGE,"E25.7");var subQ1=sQuery(id+"F0.wireOp",EDGE,"E25.1");var subQ2=sQuery(id+"F0.wireOp",EDGE,"E25.6");var subQ3=sQuery(id+"F0.wireOp",EDGE,"E25.5");var subQ4=sQuery(id+"F0.wireOp",EDGE,"E25.4");var subQ5=sQuery(id+"F0.wireOp",EDGE,"E25.0");var subQ6=sQuery(id+"F0.wireOp",EDGE,"E25.2");var subQ7=sQuery(id+"F0.wireOp",EDGE,"E25.3");Q4=makeQuery(id+"F8.boolean.opBoolean","INTERSECT",EDGE,{"derivedFrom":[makeQuery(id+"F5.boolean.opBoolean","SPLIT",FACE,{"disambiguationData":[TD([makeQuery(id+"F2.opExtrude","SWEPT_FACE",FACE,{"disambiguationData":[OSD([subQ5])]})])],"derivedFrom":makeQuery(id+"F3.boolean.opBoolean","COPY",FACE,{"derivedFrom":makeQuery(id+"F3.opExtrude","CAP_FACE",FACE,{"disambiguationData":[OSD([subQ5,subQ1,subQ6,subQ7,subQ4,subQ3,subQ2,subQ0])],"isStart":false})})}),makeQuery(id+"F8.opExtrude","SWEPT_FACE",FACE,{"disambiguationData":[OSD([sQuery(id+"F7.wireOp",EDGE,"E67")])]})]});}
            var Q5;
            Q5=makeQuery(id+"F8.boolean.opBoolean","INTERSECT",EDGE,{"disambiguationData":[OD(0.0)],"derivedFrom":[makeQuery(id+"F5.opExtrude","SWEPT_FACE",FACE,{"disambiguationData":[OSD([sQuery(id+"F4.wireOp",EDGE,"E30")])]}),makeQuery(id+"F8.opExtrude","SWEPT_FACE",FACE,{"disambiguationData":[OSD([sQuery(id+"F7.wireOp",EDGE,"E67")])]})]});
            fillet(context, id + "F14", {"entities" : qUnion([Q0, Q1, Q2, Q3, Q4, Q5]), "radius" : 3 * mm, "tangentPropagation" : true, "allowEdgeOverflow" : false});
        }
        {
            var Q0;
            Q0=makeQuery(id+"F1.opExtrude","CAP_EDGE",EDGE,{"disambiguationData":[OSD([sQuery(id+"F0.wireOp",EDGE,"E1.bottom")])],"isStart":false});
            fillet(context, id + "F15", {"entities" : qUnion([Q0]), "radius" : 2 * mm, "tangentPropagation" : true, "allowEdgeOverflow" : false});
        }
        {
            var Q0;
            {var subQ0=sQuery(id+"F0.wireOp",EDGE,"E22.filletArc");var subQ1=sQuery(id+"F0.wireOp",EDGE,"E7");var subQ2=sQuery(id+"F0.wireOp",EDGE,"E6");var subQ3=sQuery(id+"F0.wireOp",EDGE,"E5");var subQ4=sQuery(id+"F0.wireOp",EDGE,"E4");var subQ5=sQuery(id+"F0.wireOp",EDGE,"E1.bottom");var subQ6=sQuery(id+"F0.wireOp",EDGE,"E21.filletArc");var subQ7=sQuery(id+"F0.wireOp",EDGE,"E1.top");var subQ8=sQuery(id+"F0.wireOp",EDGE,"E1.left");var subQ9=sQuery(id+"F0.wireOp",EDGE,"E1.right");var subQ10=sQuery(id+"F0.wireOp",EDGE,"E23.filletArc");var subQ11=sQuery(id+"F0.wireOp",EDGE,"E24.filletArc");Q0=makeQuery(id+"F2.boolean.opBoolean","SPLIT",FACE,{"disambiguationData":[TD([makeQuery(id+"F1.opExtrude","SWEPT_FACE",FACE,{"disambiguationData":[OSD([subQ5])]})])],"derivedFrom":makeQuery(id+"F1.opExtrude","CAP_FACE",FACE,{"disambiguationData":[OSD([subQ5,subQ7,subQ8,subQ9,subQ4,subQ3,subQ2,subQ1,subQ6,subQ0,subQ10,subQ11])],"isStart":true})});}
            var sketch = newSketch(context, id + "F16", { "sketchPlane" : qUnion([Q0])});
            skCircle(sketch, "E79", {"center": v(0, 120) * mm, "radius": 6 * mm});
            skArc(sketch, "E80", {"start": v(15, 120.5) * mm, "mid": v(0, 135) * mm, "end": v(-15, 120.5) * mm});
            skLineSegment(sketch, "E81", {"start": v(15, 120.5) * mm, "end": v(15, 108) * mm});
            skLineSegment(sketch, "E82", {"start": v(0, 120) * mm, "end": v(0, 90) * mm, "construction": true});
            skLineSegment(sketch, "E83", {"start": v(0, 90) * mm, "end": v(-32.97, 90) * mm});
            skLineSegment(sketch, "E84", {"start": v(15, 108) * mm, "end": v(33, 90) * mm});
            skLineSegment(sketch, "E85.MirrorCS", {"start": v(-15, 108) * mm, "end": v(-33, 90) * mm});
            skLineSegment(sketch, "E86.MirrorCS", {"start": v(-15, 120.5) * mm, "end": v(-15, 108) * mm});
            skLineSegment(sketch, "E87", {"start": v(-80, 0) * mm, "end": v(80, 0) * mm, "construction": true});
            skArc(sketch, "E88.MirrorCS", {"start": v(15, 59.5) * mm, "mid": v(0, 45) * mm, "end": v(-15, 59.5) * mm});
            skLineSegment(sketch, "E89.MirrorCS", {"start": v(-15, -120.5) * mm, "end": v(-15, -108) * mm});
            skLineSegment(sketch, "E90.MirrorCS", {"start": v(-15, -108) * mm, "end": v(-33, -90) * mm});
            skArc(sketch, "E91.MirrorCS", {"start": v(15, -120.5) * mm, "mid": v(0, -135) * mm, "end": v(-15, -120.5) * mm});
            skLineSegment(sketch, "E92.MirrorCS", {"start": v(15, -120.5) * mm, "end": v(15, -108) * mm});
            skLineSegment(sketch, "E93.MirrorCS", {"start": v(15, -108) * mm, "end": v(33, -90) * mm});
            skCircle(sketch, "E94.MirrorC", {"center": v(0, -120) * mm, "radius": 6 * mm});
            skLineSegment(sketch, "E95.MirrorCS", {"start": v(0, -120) * mm, "end": v(0, -90) * mm, "construction": true});
            skSolve(sketch);
        }
        {
            var Q0;
            {var subQ5=sQuery(id+"F16.wireOp",EDGE,"E83");Q0=makeQuery(id+"F16.imprint","IMPRINT",FACE,{"disambiguationData":[TD([[makeQuery(id+"F16.imprint","IMPRINT",EDGE,{"derivedFrom":subQ5}),-1.0]])]});}
            var Q1;
            Q1=makeQuery(id+"F16.imprint","IMPRINT",FACE,{"disambiguationData":[TD([[makeQuery(id+"F16.imprint","IMPRINT",EDGE,{"derivedFrom":sQuery(id+"F16.wireOp",EDGE,"E89.MirrorCS")}),-1.0]])]});
            var Q2;
            Q2=makeQuery(id+"F16.imprint","IMPRINT",FACE,{"disambiguationData":[TD([[makeQuery(id+"F16.imprint","IMPRINT",EDGE,{"derivedFrom":sQuery(id+"F16.wireOp",EDGE,"E79")}),-1.0]])]});
            var Q3;
            Q3=makeQuery(id+"F2.opExtrude","CAP_FACE",FACE,{"disambiguationData":[OSD([sQuery(id+"F0.wireOp",EDGE,"E12"),sQuery(id+"F0.wireOp",EDGE,"E13"),sQuery(id+"F0.wireOp",EDGE,"E14"),sQuery(id+"F0.wireOp",EDGE,"E15"),sQuery(id+"F0.wireOp",EDGE,"E17.filletArc"),sQuery(id+"F0.wireOp",EDGE,"E18.filletArc"),sQuery(id+"F0.wireOp",EDGE,"E19.filletArc"),sQuery(id+"F0.wireOp",EDGE,"E20.filletArc"),sQuery(id+"F0.wireOp",EDGE,"E25.0"),sQuery(id+"F0.wireOp",EDGE,"E25.1"),sQuery(id+"F0.wireOp",EDGE,"E25.2"),sQuery(id+"F0.wireOp",EDGE,"E25.3"),sQuery(id+"F0.wireOp",EDGE,"E25.4"),sQuery(id+"F0.wireOp",EDGE,"E25.5"),sQuery(id+"F0.wireOp",EDGE,"E25.6"),sQuery(id+"F0.wireOp",EDGE,"E25.7")])],"isStart":false});
            extrude(context, id + "F17", {"entities" : qUnion([Q0, Q1, Q2]), "operationType" : NewBodyOperationType.ADD, "endBound" : BoundingType.UP_TO_SURFACE, "endBoundEntityFace" : qUnion([Q3]), "depth" : 25 * mm});
        }
        {
            var Q0;
            Q0=makeQuery(id+"F16.imprint","IMPRINT",FACE,{"disambiguationData":[TD([[makeQuery(id+"F16.imprint","IMPRINT",EDGE,{"derivedFrom":sQuery(id+"F16.wireOp",EDGE,"E79")}),-1.0]])]});
            var Q1;
            Q1=makeQuery(id+"F16.imprint","IMPRINT",FACE,{"disambiguationData":[TD([[makeQuery(id+"F16.imprint","IMPRINT",EDGE,{"derivedFrom":makeQuery(id+"F1.opExtrude","CAP_EDGE",EDGE,{"disambiguationData":[OSD([sQuery(id+"F0.wireOp",EDGE,"E1.left")])],"isStart":true})}),-1.0]])]});
            var Q2;
            Q2=makeQuery(id+"F16.imprint","IMPRINT",FACE,{"disambiguationData":[TD([[makeQuery(id+"F16.imprint","IMPRINT",EDGE,{"derivedFrom":sQuery(id+"F16.wireOp",EDGE,"b529e617-c95f-4df5-bdbb-58d5dbe699221.MirrorCS")}),-1.0]])]});
            var Q3;
            Q3=makeQuery(id+"F2.opExtrude","CAP_FACE",FACE,{"disambiguationData":[OSD([sQuery(id+"F0.wireOp",EDGE,"E12"),sQuery(id+"F0.wireOp",EDGE,"E13"),sQuery(id+"F0.wireOp",EDGE,"E14"),sQuery(id+"F0.wireOp",EDGE,"E15"),sQuery(id+"F0.wireOp",EDGE,"E17.filletArc"),sQuery(id+"F0.wireOp",EDGE,"E18.filletArc"),sQuery(id+"F0.wireOp",EDGE,"E19.filletArc"),sQuery(id+"F0.wireOp",EDGE,"E20.filletArc"),sQuery(id+"F0.wireOp",EDGE,"E25.0"),sQuery(id+"F0.wireOp",EDGE,"E25.1"),sQuery(id+"F0.wireOp",EDGE,"E25.2"),sQuery(id+"F0.wireOp",EDGE,"E25.3"),sQuery(id+"F0.wireOp",EDGE,"E25.4"),sQuery(id+"F0.wireOp",EDGE,"E25.5"),sQuery(id+"F0.wireOp",EDGE,"E25.6"),sQuery(id+"F0.wireOp",EDGE,"E25.7")])],"isStart":false});
            extrude(context, id + "F18", {"entities" : qUnion([Q0, Q1, Q2]), "endBound" : BoundingType.UP_TO_SURFACE, "endBoundEntityFace" : qUnion([Q3]), "depth" : 25 * mm});
        }
    });
